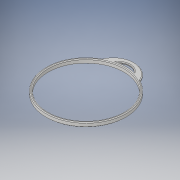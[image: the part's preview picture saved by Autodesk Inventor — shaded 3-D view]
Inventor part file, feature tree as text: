
AUTODESK INVENTOR PART (.ipt)
format: ipt  version: 2017 (Build 210142000, 142)  size: 186,880 bytes
history: native  units: in
note: dims shown in document units (in); Inventor stores cm internally (conversion verified against a paired STEP export)
features: extrude x2, sketch x2, fillet x1, projected_geometry x1
ambient origin geometry x8: Origin, YZ Plane, XZ Plane, XY Plane, X Axis, Y Axis, Z Axis, Center Point
bodies: Solid1 (feature_tree)
feature tree (6):
  extrude  "Extrusion1"  Depth=0.1181in
  extrude  "Extrusion2"  Depth=0.0394in
  fillet  "Fillet1"  Radius=0.9843in
  sketch  "Sketch1"  dims[d0=4.1339in d1=0.1181in]
  sketch  "Sketch2"  dims[d2=0.2362in d3=0.0in d4=0.2362in d5=0.9843in d6=0.1969in d7=2.082in d8=0.1181in d9=0.0in d10=0.0394in]
  projected_geometry  "Projected Loop1"
